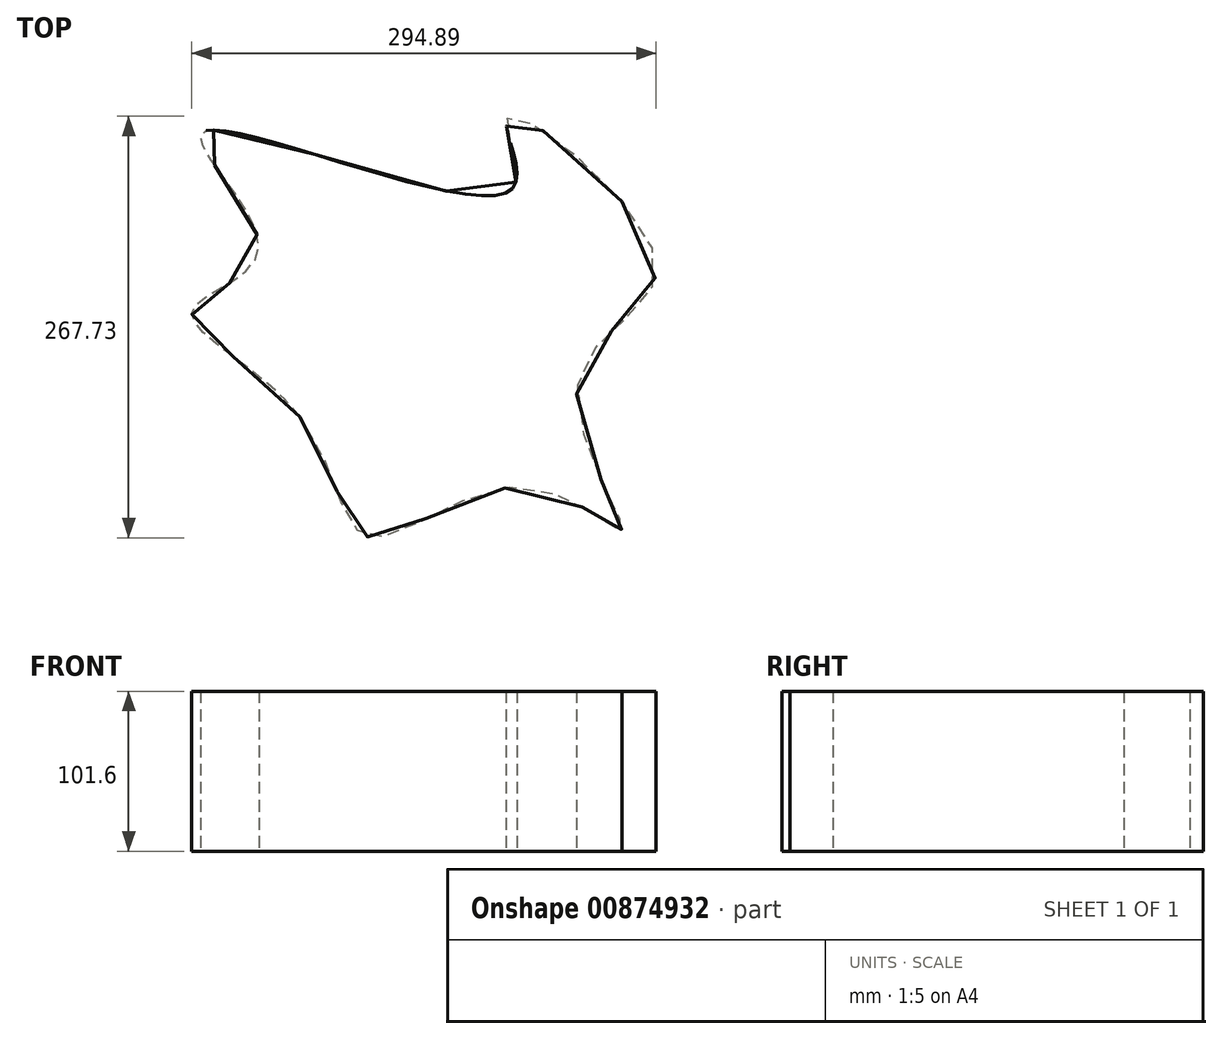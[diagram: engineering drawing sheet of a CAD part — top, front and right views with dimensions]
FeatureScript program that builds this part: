
annotation { "Feature Type Name" : "Feature", "Feature Type Description" : "" }
export const myFeature = defineFeature(function(context is Context, id is Id, definition is map)
    precondition{}
    {
        {
            var Q0;
            Q0=qCreatedBy(makeId("Top.planeOp"),FACE);
            var sketch = newSketch(context, id + "F0", { "sketchPlane" : qUnion([Q0])});
            skFitSpline(sketch, "E0", {"points": [v(-39.15, -97.98) * mm, v(-107.64, -30.14) * mm, v(-65.45, 9.1) * mm, v(-100.96, 82.76) * mm, v(94.81, 46.27) * mm, v(92.7, 92.14) * mm, v(186.61, 0) * mm, v(137.32, -74.57) * mm, v(165.12, -169.2) * mm, v(103.9, -142.6) * mm, v(4.54, -174.36) * mm, v(-39.15, -97.98) * mm]});
            skSolve(sketch);
        }
        {
            var Q0;
            Q0 = qSketchRegion(id + "F0", true);
            extrude(context, id + "F1", {"entities" : qUnion([Q0]), "depth" : 203.2 * mm, "offsetDistance" : 25.4 * mm, "hasSecondDirection" : true, "secondDirectionOppositeDirection" : false, "secondDirectionDepth" : 101.6 * mm});
        }
    });
